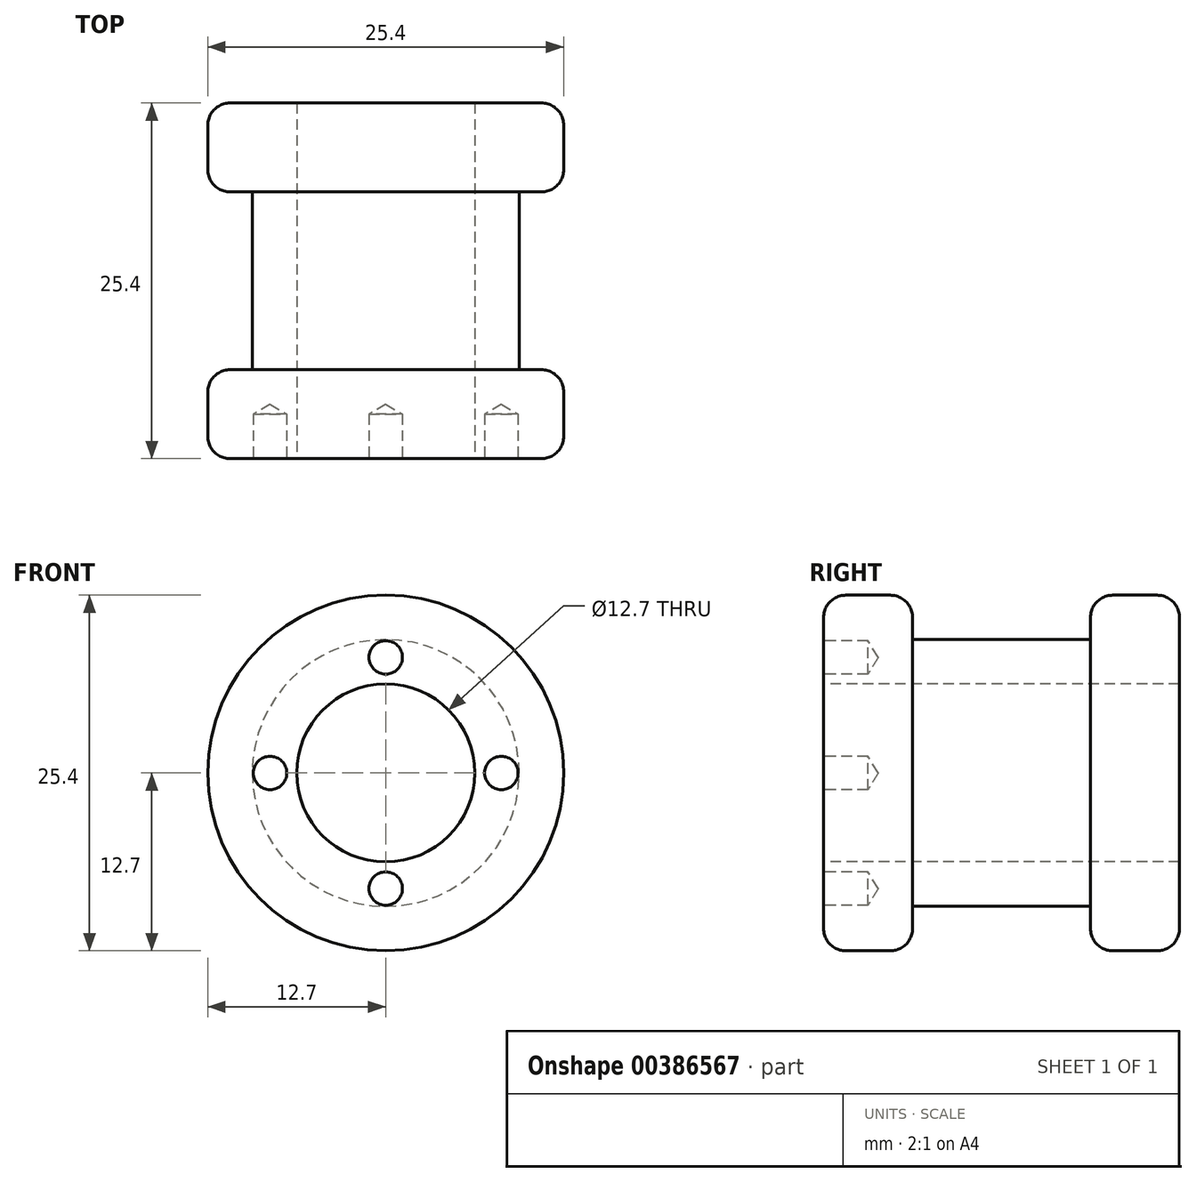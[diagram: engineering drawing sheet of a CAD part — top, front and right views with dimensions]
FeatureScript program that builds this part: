
annotation { "Feature Type Name" : "Feature", "Feature Type Description" : "" }
export const myFeature = defineFeature(function(context is Context, id is Id, definition is map)
    precondition{}
    {
        {
            var Q0;
            Q0=qCreatedBy(makeId("Front.planeOp"),FACE);
            var sketch = newSketch(context, id + "F0", { "sketchPlane" : qUnion([Q0])});
            skCircle(sketch, "E0", {"center": v(0, 0) * mm, "radius": 12.7 * mm});
            skSolve(sketch);
        }
        {
            var Q0;
            Q0 = qSketchRegion(id + "F0", true);
            extrude(context, id + "F1", {"entities" : qUnion([Q0]), "depth" : 6.35 * mm});
        }
        {
            var Q0;
            Q0=makeQuery(id+"F1.opExtrude","CAP_FACE",FACE,{"disambiguationData":[OSD([sQuery(id+"F0.wireOp",EDGE,"E0")])],"isStart":false});
            var sketch = newSketch(context, id + "F2", { "sketchPlane" : qUnion([Q0])});
            skCircle(sketch, "E1", {"center": v(0, 0) * mm, "radius": 9.53 * mm});
            skSolve(sketch);
        }
        {
            var Q0;
            Q0 = qSketchRegion(id + "F2", true);
            extrude(context, id + "F3", {"entities" : qUnion([Q0]), "operationType" : NewBodyOperationType.ADD, "depth" : 12.7 * mm});
        }
        {
            var Q0;
            Q0=makeQuery(id+"F3.opExtrude","CAP_FACE",FACE,{"disambiguationData":[OSD([sQuery(id+"F2.wireOp",EDGE,"E1")])],"isStart":false});
            var sketch = newSketch(context, id + "F4", { "sketchPlane" : qUnion([Q0])});
            skCircle(sketch, "E2", {"center": v(0, 0) * mm, "radius": 12.7 * mm});
            skSolve(sketch);
        }
        {
            var Q0;
            Q0 = qSketchRegion(id + "F4", true);
            extrude(context, id + "F5", {"entities" : qUnion([Q0]), "operationType" : NewBodyOperationType.ADD, "depth" : 6.35 * mm});
        }
        {
            var Q0;
            Q0=makeQuery(id+"F5.opExtrude","CAP_FACE",FACE,{"disambiguationData":[OSD([sQuery(id+"F4.wireOp",EDGE,"E2")])],"isStart":false});
            var sketch = newSketch(context, id + "F6", { "sketchPlane" : qUnion([Q0])});
            skPoint(sketch, "E3", {"position": v(0, 0) * mm});
            skPoint(sketch, "E4", {"position": v(0, 8.26) * mm});
            skPoint(sketch, "E5", {"position": v(0, -8.26) * mm});
            skPoint(sketch, "E6", {"position": v(8.26, 0) * mm});
            skPoint(sketch, "E7", {"position": v(-8.26, 0) * mm});
            skSolve(sketch);
        }
        {
            var Q0;
            Q0=sQuery(id+"F6.wireOp",VERTEX,"E3");
            var Q1;
            Q1=makeQuery(id+"F1.opExtrude","SWEPT_BODY",BODY,{"disambiguationData":[OSD([sQuery(id+"F0.wireOp",EDGE,"E0")])]});
            hole(context, id + "F7", {"style" : HoleStyle.SIMPLE, "endStyle" : HoleEndStyle.THROUGH, "holeDiameter" : 12.7 * mm, "isTappedThrough" : true, "tappedDepth" : 12.7 * mm, "tapClearance" : 3, "locations" : qUnion([Q0]), "scope" : qUnion([Q1])});
        }
        {
            var Q0;
            Q0=sQuery(id+"F6.wireOp",VERTEX,"E7");
            var Q1;
            Q1=sQuery(id+"F6.wireOp",VERTEX,"E4");
            var Q2;
            Q2=sQuery(id+"F6.wireOp",VERTEX,"E6");
            var Q3;
            Q3=sQuery(id+"F6.wireOp",VERTEX,"E5");
            var Q4;
            Q4=makeQuery(id+"F1.opExtrude","SWEPT_BODY",BODY,{"disambiguationData":[OSD([sQuery(id+"F0.wireOp",EDGE,"E0")])]});
            hole(context, id + "F8", {"style" : HoleStyle.SIMPLE, "endStyle" : HoleEndStyle.BLIND, "holeDiameter" : 2.4 * mm, "holeDepth" : 3.17 * mm, "isTappedThrough" : true, "tappedDepth" : 12.7 * mm, "tapClearance" : 3, "locations" : qUnion([Q0, Q1, Q2, Q3]), "scope" : qUnion([Q4])});
        }
        {
            var Q0;
            Q0=makeQuery(id+"F5.opExtrude","CAP_EDGE",EDGE,{"disambiguationData":[OSD([sQuery(id+"F4.wireOp",EDGE,"E2")])],"isStart":false});
            var Q1;
            Q1=makeQuery(id+"F5.opExtrude","CAP_EDGE",EDGE,{"disambiguationData":[OSD([sQuery(id+"F4.wireOp",EDGE,"E2")])],"isStart":true});
            var Q2;
            Q2=makeQuery(id+"F1.opExtrude","CAP_EDGE",EDGE,{"disambiguationData":[OSD([sQuery(id+"F0.wireOp",EDGE,"E0")])],"isStart":false});
            var Q3;
            Q3=makeQuery(id+"F1.opExtrude","CAP_EDGE",EDGE,{"disambiguationData":[OSD([sQuery(id+"F0.wireOp",EDGE,"E0")])],"isStart":true});
            var Q4;
            Q4=makeQuery(id+"F3.opExtrude","CAP_EDGE",EDGE,{"disambiguationData":[OSD([sQuery(id+"F2.wireOp",EDGE,"E1")])],"isStart":true});
            var Q5;
            Q5=makeQuery(id+"F3.opExtrude","CAP_EDGE",EDGE,{"disambiguationData":[OSD([sQuery(id+"F2.wireOp",EDGE,"E1")])],"isStart":false});
            fillet(context, id + "F9", {"entities" : qUnion([Q0, Q1, Q2, Q3, Q4, Q5]), "radius" : 1.59 * mm, "tangentPropagation" : true, "allowEdgeOverflow" : false});
        }
    });
